# Revit family: Bernhardt_Design-Seating-Lounge-Jackson
name_source: partatom
category: Furniture
revit_build: Autodesk Revit 2016 (Build: 20150714_1515(x64)
units: mm (PartAtom-declared; Revit-internal decimal feet)

## family parameters
Always vertical = Yes
Cut with Voids When Loaded = No
OmniClass Number = 23.40.20.00
OmniClass Title = General Furniture and Specialties
Room Calculation Point = No
Shared = No
Work Plane-Based = No

## types (6) — shared parameters
Base material = Casters
Casters material = Casters
Manufacturer = Bernhardt Design
Metal material = Aluminum - Matte Black Powdercoat
Model = Jackson
URL = http://www.bernhardtdesign.com

## per-type parameters (varying)
| type | Base | Casters | Catalog | Table - left | Table - right | base height |
| Jackson 4681 | No | Yes | 4681 | No | No | 0' - 2 29/32" |
| Jackson 4680 | Yes | No | 4680 | No | No | 0' - 0 13/32" |
| Jackson 4681L | No | Yes | 4681L | No | Yes | 0' - 2 29/32" |
| Jackson 4681R | No | Yes | 4681R | Yes | No | 0' - 2 29/32" |
| Jackson 4680R | Yes | No | 4680R | Yes | No | 0' - 0 13/32" |
| Jackson 4680L | Yes | No | 4680L | No | Yes | 0' - 0 13/32" |

## geometry (parser evidence)
native form markers: Sweep x5
no freeform markers — native parametric forms only
